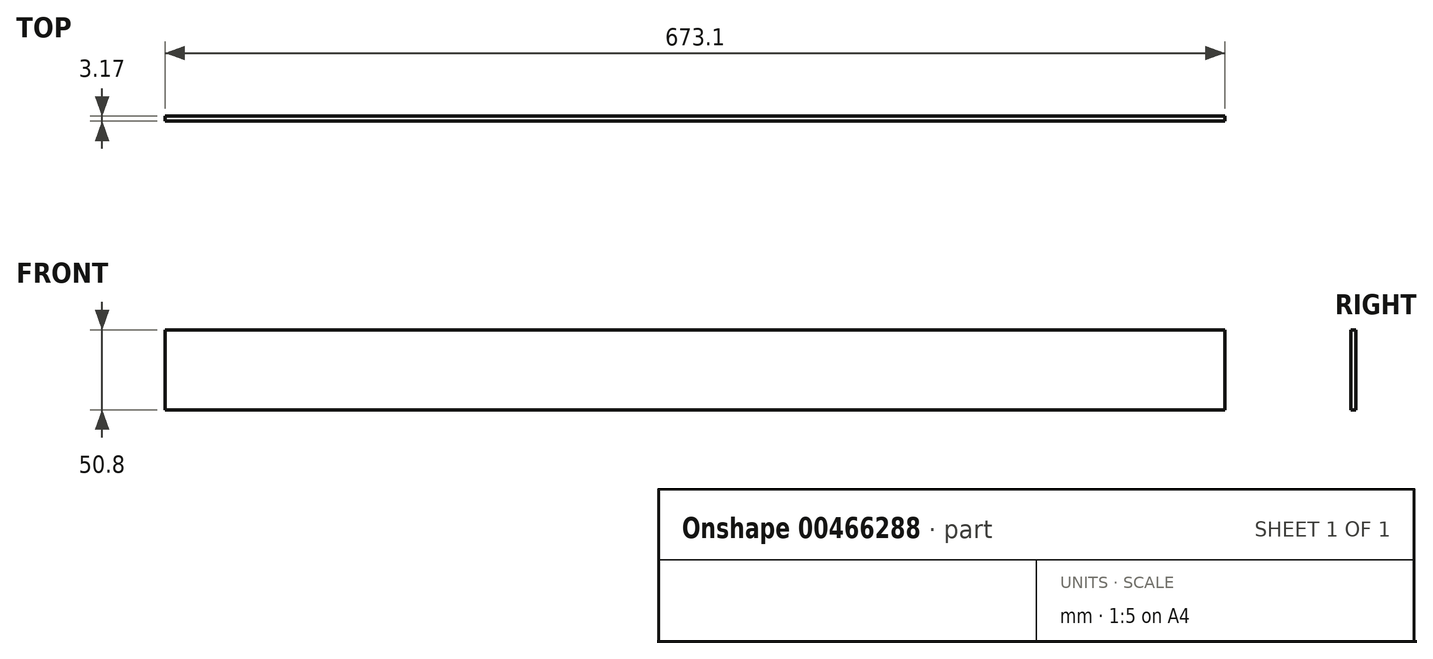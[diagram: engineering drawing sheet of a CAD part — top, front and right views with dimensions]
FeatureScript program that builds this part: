
annotation { "Feature Type Name" : "Feature", "Feature Type Description" : "" }
export const myFeature = defineFeature(function(context is Context, id is Id, definition is map)
    precondition{}
    {
        {
            var Q0;
            Q0=qCreatedBy(makeId("Front.planeOp"),FACE);
            var sketch = newSketch(context, id + "F0", { "sketchPlane" : qUnion([Q0])});
            skLineSegment(sketch, "E0", {"start": v(-367.72, 137.46) * mm, "end": v(305.38, 137.46) * mm});
            skLineSegment(sketch, "E1", {"start": v(305.38, 137.46) * mm, "end": v(305.38, 86.66) * mm});
            skLineSegment(sketch, "E2", {"start": v(305.38, 86.66) * mm, "end": v(-367.72, 86.66) * mm});
            skLineSegment(sketch, "E3", {"start": v(-367.72, 86.66) * mm, "end": v(-367.72, 137.46) * mm});
            skSolve(sketch);
        }
        {
            var Q0;
            Q0=qSketchRegion(id+"F0",true);
            extrude(context, id + "F1", {"entities" : qUnion([Q0]), "depth" : 3.17 * mm, "offsetDistance" : 25.4 * mm});
        }
    });
